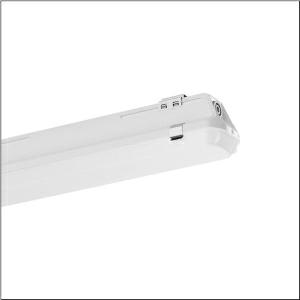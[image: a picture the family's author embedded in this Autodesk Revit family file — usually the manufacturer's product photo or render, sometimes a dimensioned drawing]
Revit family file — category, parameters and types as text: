
# Revit family: monsun_r__11_emergency_51fp207p467h3g_ea6c
name_source: partatom
category: Lighting Fixtures
units: mm (PartAtom-declared; Revit-internal decimal feet)

## family parameters
Cut with Voids When Loaded = No
Host = Face
Light Source = No
Part Type = Normal
Room Calculation Point = No
Round Connector Dimension = Use Diameter
Shared = No

## types (1)
- Monsun® 11 emergency (1 x LED, 5450 lm, 37.2 W, 4000K)
    Apparent Load = 37 VA
    CIE Flux Codes = 45 75 93 94 100
    Color Rendering = 80
    Color Temperature = 4000K
    Default Elevation = 1800 mm
    Description = Monsun® 11 emergency, damp-proof luminaire, chain hanger, primary optical cover: enclosure, of PC, light emission: direct distribution, primary light characteristic: symmetric, installation type: suspended mounting, surface-mounted, horizontal mounting, vertical mounting, LED, rated luminous flux: 5.450lm, luminous efficacy: 147lm/W, light colour: 840, colour temperature: 4000K, control gear: ECG, with terminal, 4-pole, max. 2.5mm², mains connection: 220..240V, AC, 50/60Hz, rated input power: 37W, control gear: single battery element, battery: NiCd, 4,5Ah, mains connection: 230V, luminaire housing, of glass-fibre reinforced polyester, uncoated, bright grey, incl. chain hanger, length: 1.590mm, width: 90mm, height: 88mm, clip for enclosure, of stainless steel (V2A), ceiling mounting element, of stainless steel (V2A), chain hanger, of stainless steel (V2A), protection rating (complete): IP66, insulation class (complete): insulation class I (protective earthing), certification: CE, UKCA, protection symbol: D, impact resistance: IK08, permissible operating ambient temperature: +5..+35°C, standard: EN 50419, EN 60598-2-1, EN 60598-2-22, no direct snow, no direct sun, no direct rain, for indoor or canopied outdoor use, corresponds to IFS (International Featured Standards) requirements for safety and quality in the food industry, contact your sales advisor before using the luminaires in applications with unclear chemical exposure, large temperature fluctuations or condensation-forming humidity, LABS conformity tested according to VDMA 24364:2018-05, packaging unit: 1 piece
    Height = 89 mm
    Lamp = 1 x LED
    Lamp Light Flux = 5450 lm
    Lamp Power = 37.2 W
    Lamp count = 1
    Length = 1590 mm
    Luminous efficacy = 147 lm/W
    Manufacturer = Siteco
    ModVariant = No
    Model = 51FP207P467H3G
    Mounting Place = Ceiling
    Mounting Type = Surface mounted
    Number of Poles = 1
    OnlyDefault = Yes
    Power Factor = 1
    Product Name = Monsun® 11 emergency
    Product group = damp-proof luminaire
    ProductGroupID = 301
    Protection Class = Protection class I
    Protection Degree = IP 66
    RLX_Detail_Level = 1
    RLX_Emergency_Light_Flux = 0 lm
    RLX_Emergency_Type = 0
    RLX_Emergency_Type_DB = No
    RlxData = <blob elided: 89081 chars, md5=e5de6485>
    Socket = socket
    Standby Power = 0 W
    System Light Flux = 5450 lm
    System Power = 37 W
    Type Comments = Product without accessories
    Type Image = l_1004748.jpg
    URL = http://relux.com
    VarID = ---
    Voltage = 0 V
    Weight = 0.00 kg
    Width = 90 mm

## geometry (parser evidence)
native form markers: Blend x4, Sweep x13
no freeform markers — native parametric forms only
